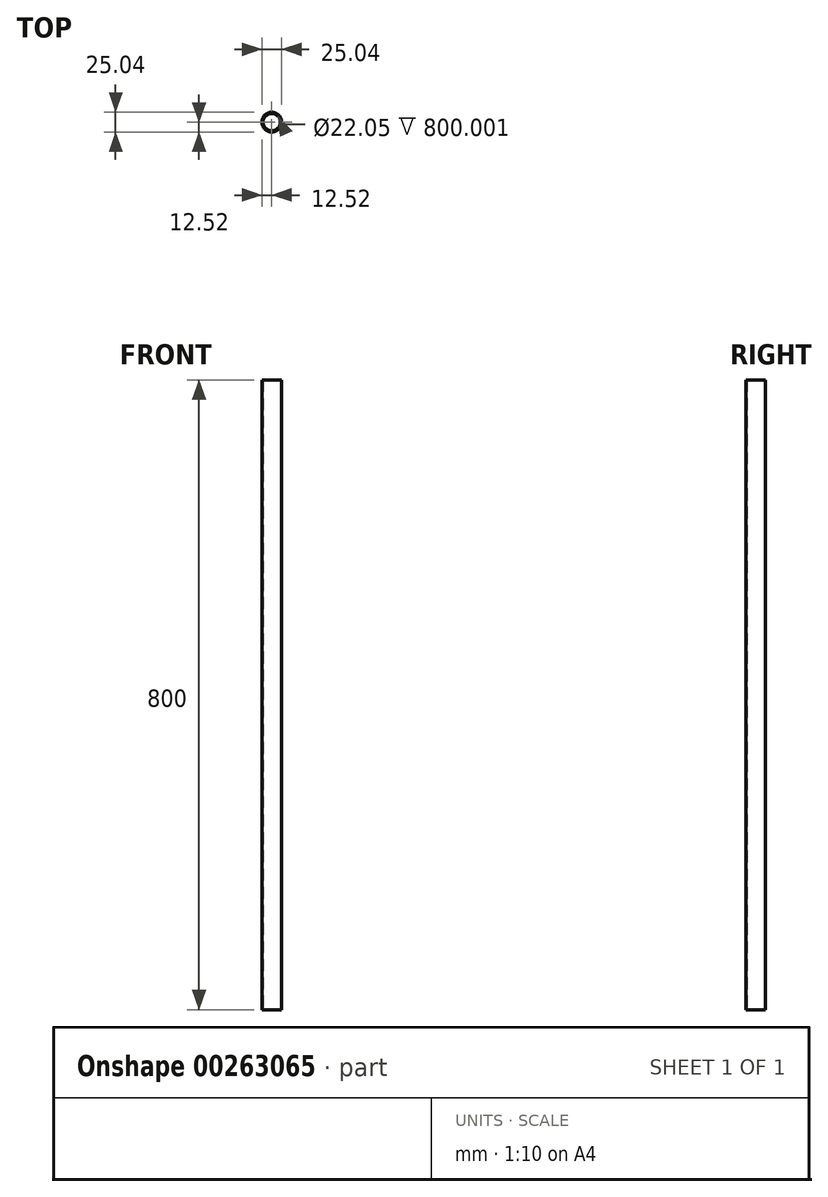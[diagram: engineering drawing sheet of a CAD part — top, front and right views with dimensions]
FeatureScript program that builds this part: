
annotation { "Feature Type Name" : "Feature", "Feature Type Description" : "" }
export const myFeature = defineFeature(function(context is Context, id is Id, definition is map)
    precondition{}
    {
        {
            var Q0;
            Q0=qCreatedBy(makeId("Top.planeOp"),FACE);
            var sketch = newSketch(context, id + "F0", { "sketchPlane" : qUnion([Q0])});
            skCircle(sketch, "E0", {"center": v(0, 0) * mm, "radius": 11.02 * mm});
            skCircle(sketch, "E1", {"center": v(0, 0) * mm, "radius": 12.52 * mm});
            skSolve(sketch);
        }
        {
            var Q0;
            Q0=makeQuery(id+"F0.imprint","IMPRINT",FACE,{"disambiguationData":[TD([[makeQuery(id+"F0.imprint","IMPRINT",EDGE,{"derivedFrom":sQuery(id+"F0.wireOp",EDGE,"E0")}),-1.0]])]});
            extrude(context, id + "F1", {"entities" : qUnion([Q0]), "depth" : 800 * mm});
        }
    });
